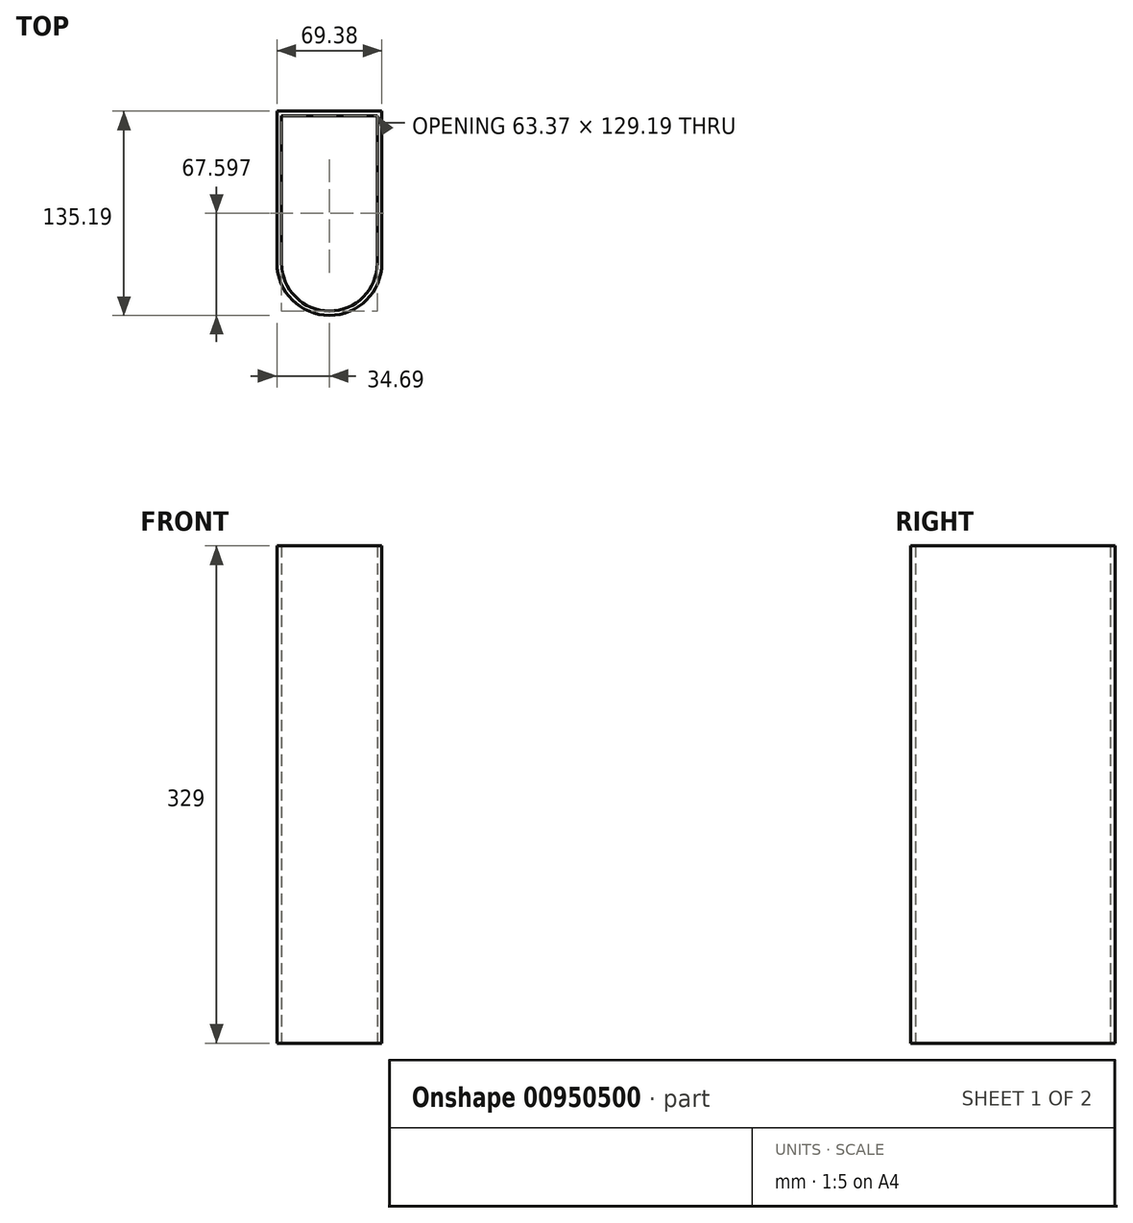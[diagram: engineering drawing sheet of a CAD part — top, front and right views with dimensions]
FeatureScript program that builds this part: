
annotation { "Feature Type Name" : "Feature", "Feature Type Description" : "" }
export const myFeature = defineFeature(function(context is Context, id is Id, definition is map)
    precondition{}
    {
        {
            var Q0;
            Q0=qCreatedBy(makeId("Top.planeOp"),FACE);
            var sketch = newSketch(context, id + "F0", { "sketchPlane" : qUnion([Q0])});
            skCircle(sketch, "E0", {"center": v(0, 0) * mm, "radius": 10.5 * mm});
            skCircle(sketch, "E1.0.1.0", {"center": v(0, 21) * mm, "radius": 10.5 * mm});
            skCircle(sketch, "E1.0.2.0", {"center": v(0, 42) * mm, "radius": 10.5 * mm});
            skCircle(sketch, "E1.0.3.0", {"center": v(0, 63) * mm, "radius": 10.5 * mm});
            skLineSegment(sketch, "E1.direction1", {"start": v(0, 0) * mm, "end": v(23.24, 0) * mm, "construction": true});
            skLineSegment(sketch, "E1.direction2", {"start": v(0, 0) * mm, "end": v(0, 21) * mm, "construction": true});
            skCircle(sketch, "E2", {"center": v(18.19, 10.5) * mm, "radius": 10.5 * mm});
            skCircle(sketch, "E3.0.1.0", {"center": v(18.19, 31.5) * mm, "radius": 10.5 * mm});
            skCircle(sketch, "E3.0.2.0", {"center": v(18.19, 52.5) * mm, "radius": 10.5 * mm});
            skCircle(sketch, "E3.0.3.0", {"center": v(18.19, 73.5) * mm, "radius": 10.5 * mm});
            skLineSegment(sketch, "E3.direction1", {"start": v(18.19, 10.5) * mm, "end": v(41.42, 10.5) * mm, "construction": true});
            skLineSegment(sketch, "E3.direction2", {"start": v(18.19, 10.5) * mm, "end": v(18.19, 31.5) * mm, "construction": true});
            skCircle(sketch, "E4", {"center": v(-18.19, 10.5) * mm, "radius": 10.5 * mm});
            skCircle(sketch, "E5.0.1.0", {"center": v(-18.19, 31.5) * mm, "radius": 10.5 * mm});
            skCircle(sketch, "E5.0.2.0", {"center": v(-18.19, 52.5) * mm, "radius": 10.5 * mm});
            skCircle(sketch, "E5.0.3.0", {"center": v(-18.19, 73.5) * mm, "radius": 10.5 * mm});
            skLineSegment(sketch, "E5.direction1", {"start": v(-18.19, 10.5) * mm, "end": v(7.65, 10.5) * mm, "construction": true});
            skLineSegment(sketch, "E5.direction2", {"start": v(-18.19, 10.5) * mm, "end": v(-18.19, 31.5) * mm, "construction": true});
            skLineSegment(sketch, "E6", {"start": v(0, -10.5) * mm, "end": v(0, 94.5) * mm, "construction": true});
            skCircle(sketch, "E7.0.0.4", {"center": v(0, 84) * mm, "radius": 10.5 * mm});
            skCircle(sketch, "E8", {"center": v(-18.19, 94.5) * mm, "radius": 10.5 * mm});
            skCircle(sketch, "E9", {"center": v(18.19, 94.5) * mm, "radius": 10.5 * mm});
            skSolve(sketch);
        }
        {
            var Q0;
            Q0=qCreatedBy(makeId("Top.planeOp"),FACE);
            var sketch = newSketch(context, id + "F1", { "sketchPlane" : qUnion([Q0])});
            skLineSegment(sketch, "E10", {"start": v(-31.69, 108) * mm, "end": v(31.69, 108) * mm});
            skLineSegment(sketch, "E11", {"start": v(31.69, 108) * mm, "end": v(31.69, 10.5) * mm});
            skLineSegment(sketch, "E12", {"start": v(-31.69, 108) * mm, "end": v(-31.69, 10.5) * mm});
            skArc(sketch, "E13", {"start": v(-31.69, 10.5) * mm, "mid": v(0, -21.19) * mm, "end": v(31.69, 10.5) * mm});
            skLineSegment(sketch, "E14.0", {"start": v(-34.69, 111) * mm, "end": v(34.69, 111) * mm});
            skLineSegment(sketch, "E14.1", {"start": v(-34.69, 111) * mm, "end": v(-34.69, 10.5) * mm});
            skArc(sketch, "E14.2", {"start": v(-34.69, 10.5) * mm, "mid": v(0, -24.19) * mm, "end": v(34.69, 10.5) * mm});
            skLineSegment(sketch, "E14.3", {"start": v(34.69, 111) * mm, "end": v(34.69, 10.5) * mm});
            skSolve(sketch);
        }
        {
            var Q0;
            Q0 = qSketchRegion(id + "F1", true);
            extrude(context, id + "F2", {"entities" : qUnion([Q0]), "depth" : (76 * 4) * mm + 25 * mm, "offsetDistance" : 25 * mm});
        }
    });
